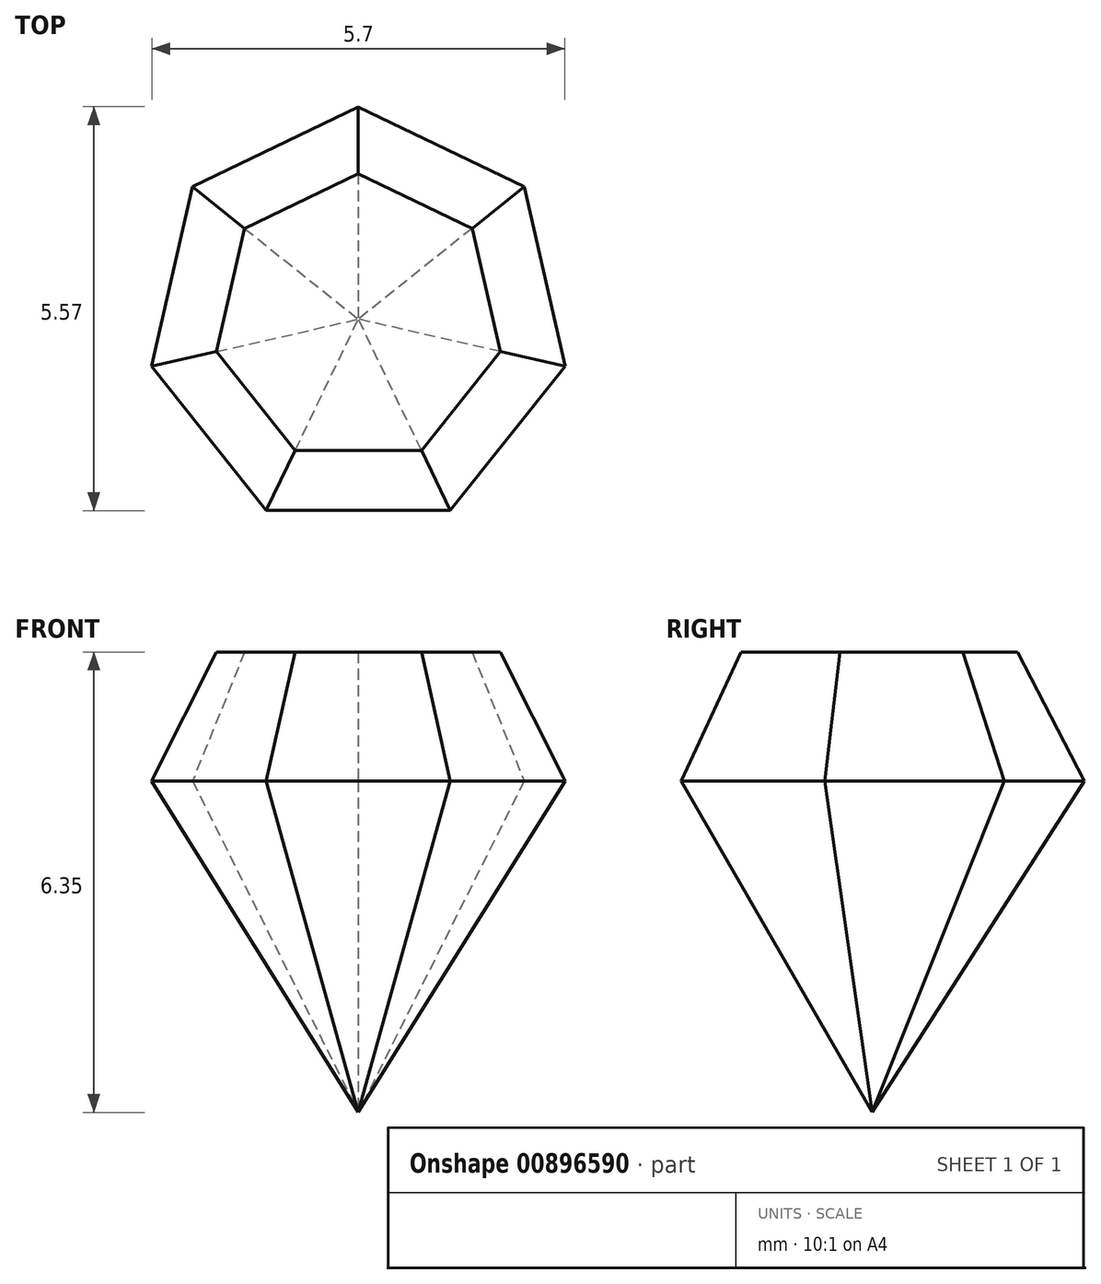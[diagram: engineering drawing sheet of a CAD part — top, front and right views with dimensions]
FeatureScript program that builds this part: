
annotation { "Feature Type Name" : "Feature", "Feature Type Description" : "" }
export const myFeature = defineFeature(function(context is Context, id is Id, definition is map)
    precondition{}
    {
        {
            var Q0;
            Q0=qCreatedBy(makeId("Top.planeOp"),FACE);
            var sketch = newSketch(context, id + "F0", { "sketchPlane" : qUnion([Q0])});
            skCircle(sketch, "E0.cCircle", {"center": v(0, 0) * mm, "radius": 2.64 * mm, "construction": true});
            skLineSegment(sketch, "E0.0", {"start": v(2.85, -0.65) * mm, "end": v(1.27, -2.64) * mm});
            skLineSegment(sketch, "E0.1", {"start": v(1.27, -2.64) * mm, "end": v(-1.27, -2.64) * mm});
            skLineSegment(sketch, "E0.2", {"start": v(-1.27, -2.64) * mm, "end": v(-2.85, -0.65) * mm});
            skLineSegment(sketch, "E0.3", {"start": v(-2.85, -0.65) * mm, "end": v(-2.29, 1.82) * mm});
            skLineSegment(sketch, "E0.4", {"start": v(-2.29, 1.82) * mm, "end": v(0, 2.93) * mm});
            skLineSegment(sketch, "E0.5", {"start": v(0, 2.93) * mm, "end": v(2.29, 1.82) * mm});
            skLineSegment(sketch, "E0.6", {"start": v(2.29, 1.82) * mm, "end": v(2.85, -0.65) * mm});
            skPoint(sketch, "E0.0.midPoint", {"position": v(2.06, -1.64) * mm});
            skSolve(sketch);
        }
        {
            var Q0;
            Q0=makeQuery(id+"F0.imprint","IMPRINT",FACE,{"disambiguationData":[TD([[makeQuery(id+"F0.imprint","IMPRINT",EDGE,{"derivedFrom":sQuery(id+"F0.wireOp",EDGE,"E0.0")}),-1.0]])]});
            extrude(context, id + "F1", {"entities" : qUnion([Q0]), "depth" : 1.78 * mm, "offsetDistance" : 25.4 * mm, "hasDraft" : true, "draftAngle" : 25 * degree, "draftPullDirection" : true, "hasSecondDirection" : true, "secondDirectionOppositeDirection" : true, "secondDirectionDepth" : 4.6 * mm, "hasSecondDirectionDraft" : true, "secondDirectionDraftAngle" : 30 * degree, "secondDirectionDraftPullDirection" : true});
        }
    });
